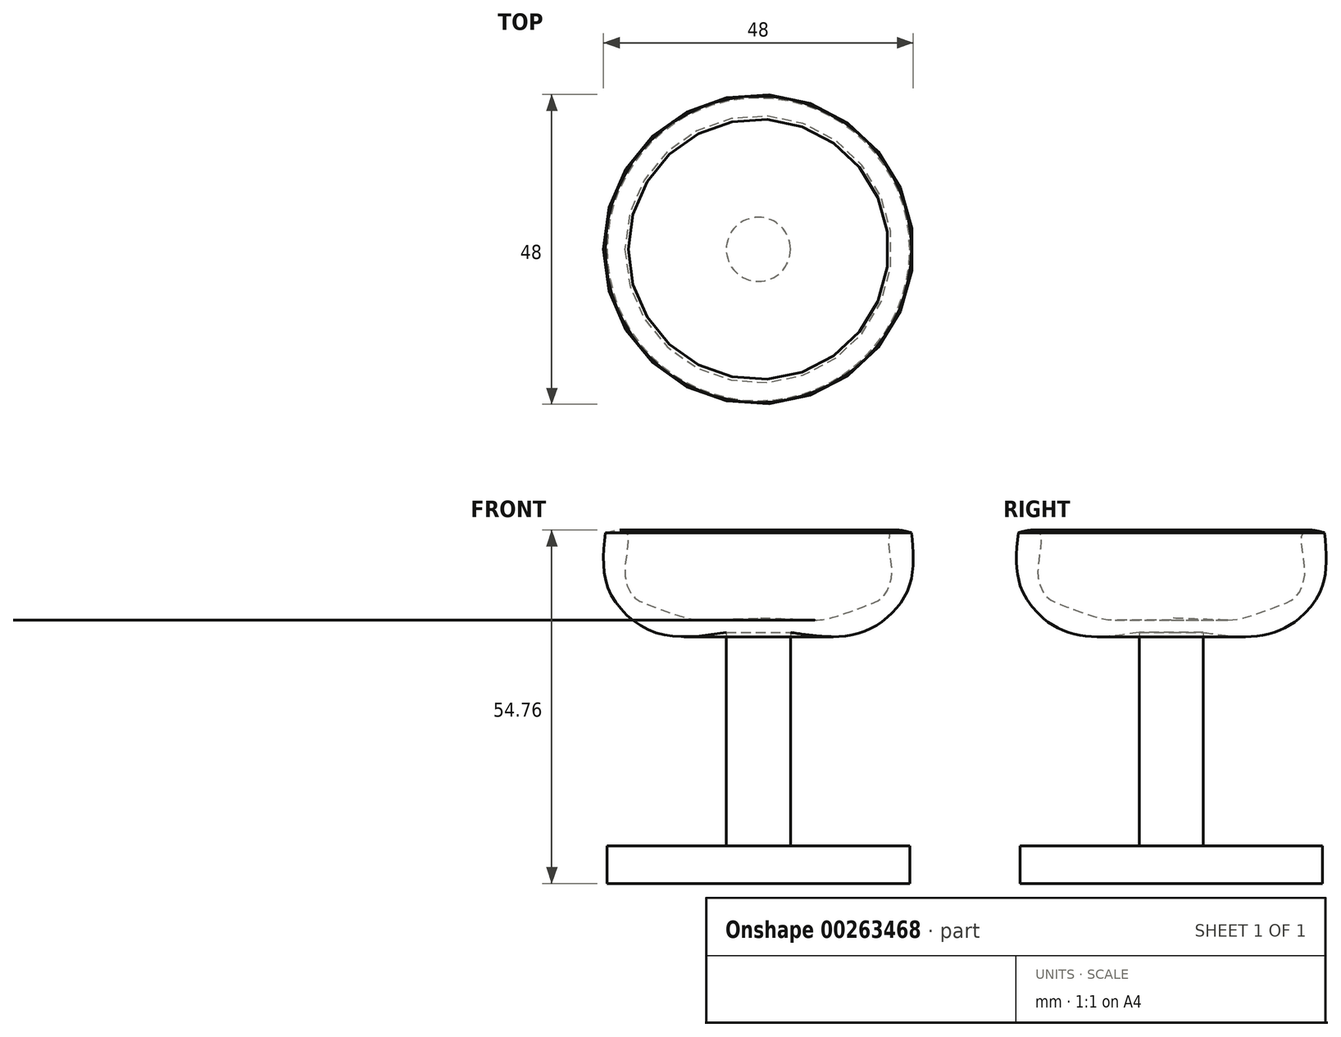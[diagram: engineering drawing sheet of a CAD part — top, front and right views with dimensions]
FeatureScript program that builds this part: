
annotation { "Feature Type Name" : "Feature", "Feature Type Description" : "" }
export const myFeature = defineFeature(function(context is Context, id is Id, definition is map)
    precondition{}
    {
        {
            var Q0;
            Q0=qCreatedBy(makeId("Front.planeOp"),FACE);
            var sketch = newSketch(context, id + "F0", { "sketchPlane" : qUnion([Q0])});
            skLineSegment(sketch, "E0", {"start": v(0, 0) * mm, "end": v(0, 75.6) * mm, "construction": true});
            skLineSegment(sketch, "E1", {"start": v(0, 0) * mm, "end": v(-23.45, 0) * mm});
            skLineSegment(sketch, "E2", {"start": v(-23.45, 0) * mm, "end": v(-23.45, 5.8) * mm});
            skLineSegment(sketch, "E3", {"start": v(-23.45, 5.8) * mm, "end": v(-4.97, 5.8) * mm});
            skLineSegment(sketch, "E4", {"start": v(-4.97, 5.8) * mm, "end": v(-4.97, 38.9) * mm});
            skFitSpline(sketch, "E5", {"points": [v(-4.97, 38.9) * mm, v(-16, 38.9) * mm, v(-23.18, 45.52) * mm, v(-23.73, 54.35) * mm], "startDerivative": vector(-32.55, -4.92) * mm, "endDerivative": vector(2.81, 28.79) * mm});
            skFitSpline(sketch, "E6", {"points": [v(-23.73, 54.35) * mm, v(-20.42, 54.35) * mm, v(-20.7, 48.28) * mm, v(-19.31, 44.42) * mm, v(-17.38, 43.32) * mm, v(-11.04, 41.1) * mm, v(-8, 40.83) * mm, v(0, 41.1) * mm], "startDerivative": vector(34.65, 8.74) * mm, "endDerivative": vector(48.75, 1.84) * mm});
            skLineSegment(sketch, "E7", {"start": v(0, 41.1) * mm, "end": v(0, 0) * mm});
            skSolve(sketch);
        }
        {
            var Q0;
            Q0=makeQuery(id+"F0.imprint","IMPRINT",FACE,{"disambiguationData":[TD([[makeQuery(id+"F0.imprint","IMPRINT",EDGE,{"derivedFrom":sQuery(id+"F0.wireOp",EDGE,"E1")}),-1.0]])]});
            var Q1;
            Q1=sQuery(id+"F0.wireOp",EDGE,"E0");
            revolve(context, id + "F1", {"entities" : qUnion([Q0]), "axis" : qUnion([Q1]), "revolveType" : RevolveType.FULL});
        }
    });
